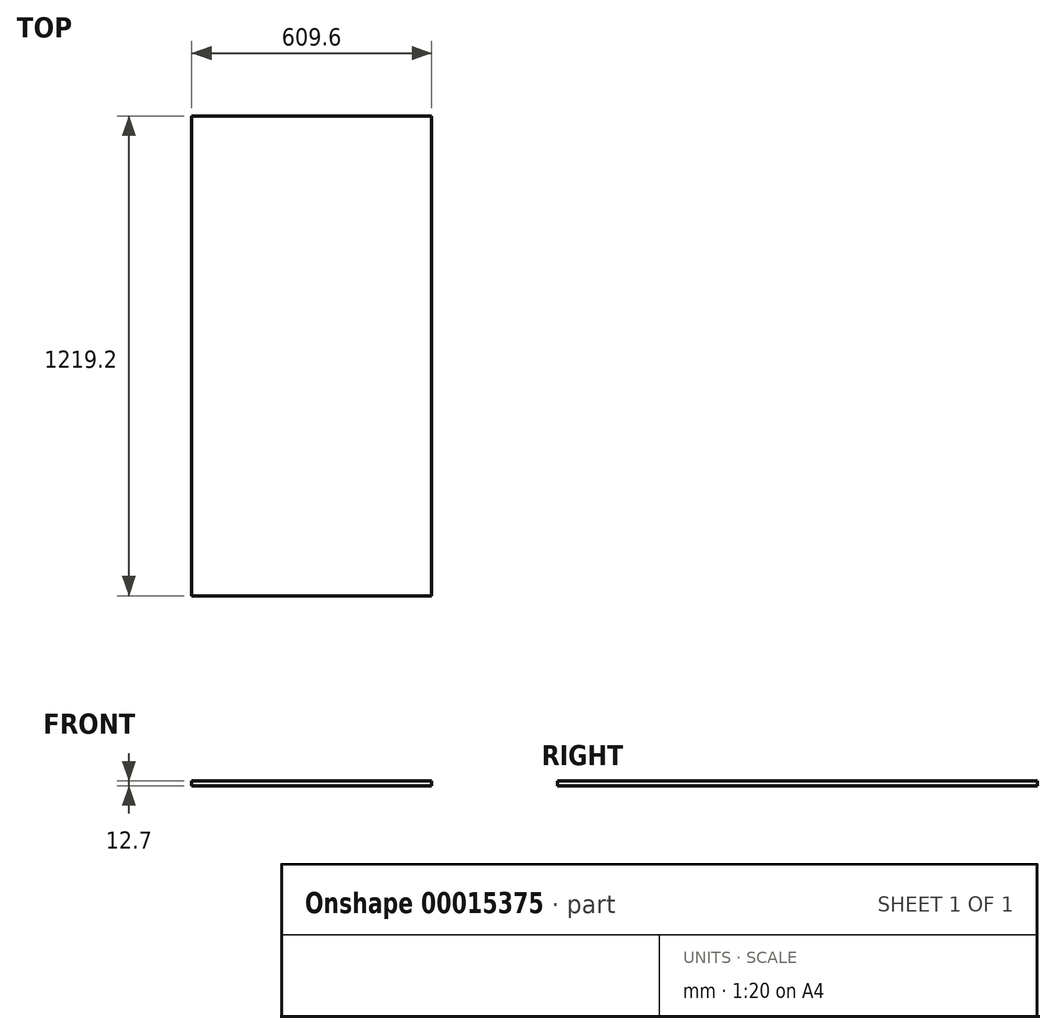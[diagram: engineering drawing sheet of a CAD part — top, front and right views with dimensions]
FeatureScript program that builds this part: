
annotation { "Feature Type Name" : "Feature", "Feature Type Description" : "" }
export const myFeature = defineFeature(function(context is Context, id is Id, definition is map)
    precondition{}
    {
        {
            var Q0;
            Q0=qCreatedBy(makeId("Top.planeOp"),FACE);
            var sketch = newSketch(context, id + "F0", { "sketchPlane" : qUnion([Q0])});
            skLineSegment(sketch, "E0.bottom", {"start": v(0, 0) * mm, "end": v(609.6, 0) * mm});
            skLineSegment(sketch, "E0.top", {"start": v(0, 1219.2) * mm, "end": v(609.6, 1219.2) * mm});
            skLineSegment(sketch, "E0.left", {"start": v(0, 0) * mm, "end": v(0, 1219.2) * mm});
            skLineSegment(sketch, "E0.right", {"start": v(609.6, 0) * mm, "end": v(609.6, 1219.2) * mm});
            skSolve(sketch);
        }
        {
            var Q0;
            Q0=makeQuery(id+"F0.imprint","IMPRINT",FACE,{"disambiguationData":[TD([[makeQuery(id+"F0.imprint","IMPRINT",EDGE,{"derivedFrom":sQuery(id+"F0.wireOp",EDGE,"E0.bottom")}),1.0]])]});
            extrude(context, id + "F1", {"entities" : qUnion([Q0]), "depth" : 12.7 * mm});
        }
    });
